# Revit family: 1403009 Lynx Recess - Matt White - 30°
name_source: partatom
category: Lighting Fixtures
units: mm (PartAtom-declared; Revit-internal decimal feet)

## family parameters
Always vertical = Yes
Cut with Voids When Loaded = No
Host = Ceiling
Light Source = Yes
OmniClass Number = 23.80.70.11
OmniClass Title = Luminaries for Internal Lighting
Part Type = Normal
Room Calculation Point = No
Round Connector Dimension = Use Diameter
Shared = No

## types (2) — shared parameters
Apparent Load = 0 VA
Color Filter = 16777215
Dimming Lamp Color Temperature Shift = <None>
Emit Shape Visible in Rendering = No
Manufacturer URL - Europe and Rest of World = www.astrolighting.com
Manufacturer URL - North America = us.astrolighting.com
zero-valued in all types: Default Elevation

## per-type parameters (varying)
| type | ADA compliant | Dimmable | Dimming Method | Driver Included | Driver Required | Efficacy (lm/w) | Electrical Class | Emit from Circle Diameter | Lamp | Light Source Fixed | Location / IP Rating | Main Finish | Main Material | Photometric Web File | Power (Watts) | Product CCT | Product CRI | Product Dimensions (MM) | Product Location | Product Name | Product SKU | Product Weight (KG) | Tilt Angle |
| CE | Not Applicable | Yes | Phase - Leading Edge | Yes (Integral) | No | 67 | 1 | 1 mm  [stored 0.00328084 ft] | LED | No | IP20 | Matt White | Metal - Aluminium | 1403009_Lynx Recess Matt White_Photometry_IES_Iss. 01.ies | 12.1 | 3000K | 80 | 156 x Ø100 | Architectural, Indoor | Lynx Recess | 1403009 | 1 mm  [stored 0.00328084 ft] | 30.00° |
| ETL |  |  |  |  |  |  |  | 610 mm |  |  |  |  |  | 1403006_Lynx Matt Black_Photometry_IES_Iss. 01.ies |  | 2700K / 3000K | 80/ 90 |  |  |  | 1234567 | 0 mm  [stored 0 ft] | 60.00° |

note: [stored X ft] marks values corroborated as IEEE doubles in the binary element streams (Revit-internal decimal feet)

## geometry (parser evidence)
native form markers: Sweep x3
no freeform markers — native parametric forms only
